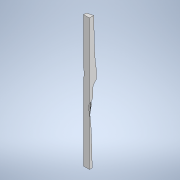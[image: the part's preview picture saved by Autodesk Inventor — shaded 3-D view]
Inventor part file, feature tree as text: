
AUTODESK INVENTOR PART (.ipt)
format: ipt  version: 2022 (Build 260153000, 153)  size: 1,856,000 bytes
history: native  units: mm
features: sketch x11, sweep x4, other x3, extrude x1, boolean_combine x1, surface_op x1, split x1
ambient origin geometry x8: Origin, YZ Plane, XZ Plane, XY Plane, X Axis, Y Axis, Z Axis, Center Point
bodies: Solid4 (feature_tree), Solid5 (feature_tree)
feature tree (22):
  sketch  "Sketch1"  dims[d14=330.0mm d15=0.0mm d16=0.0mm]
  sketch  "Sketch2"  dims[d17=330.0mm d18=90.0deg]
  sketch  "3D Sketch1"
  sketch  "3D Sketch2"
  sweep  "Sweep4"
  sweep  "Sweep5"
  extrude  "Extrusion1"  Depth=30.0mm
  boolean_combine  "Combine1"
  sketch  "Sketch6"  dims[d30=100.0mm d31=0.0mm]
  sketch  "Sketch7"  dims[d32=380.0mm]
  sketch  "Sketch8"  dims[d33=380.0mm d34=0.0mm d35=0.0mm d36=0.0mm d37=0.0mm]
  surface_op  "Stitch Surface1"
  split  "Split1"
  sketch  "Sketch4"  dims[d19=0.0mm d20=0.0mm d21=30.0mm]
  sketch  "Sketch5"  dims[d22=670.0mm d23=36.0mm d24=0.0mm]
  sketch  "3D Sketch4"
  other  "Srf5"
  sketch  "3D Sketch5"
  other  "Srf6"
  other  "Srf7"
  sweep  "SweepSrf1"
  sweep  "SweepSrf2"
